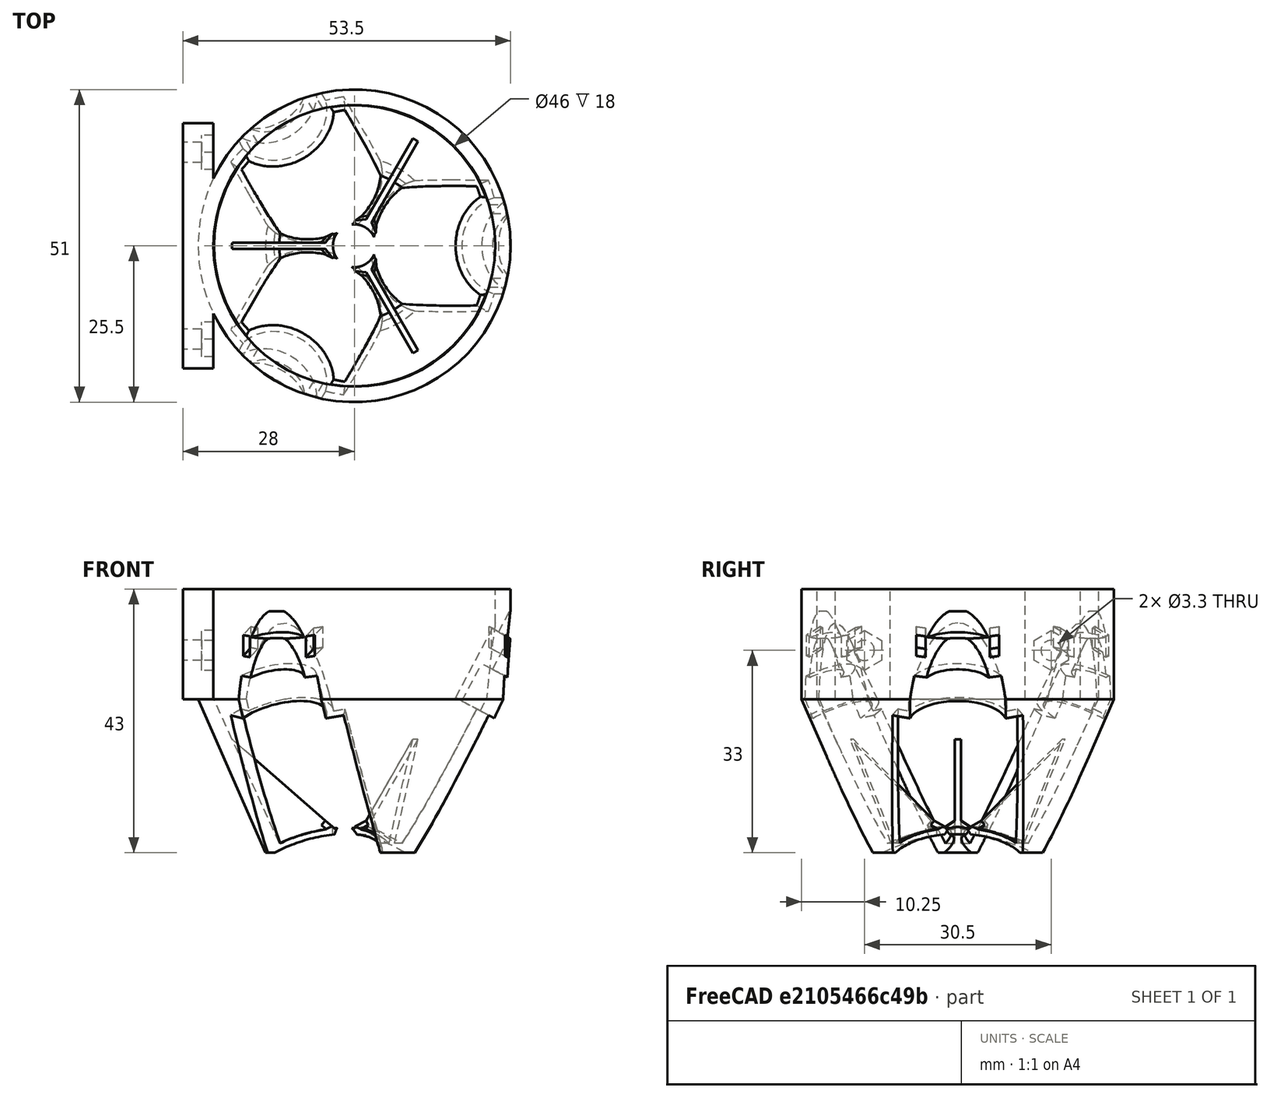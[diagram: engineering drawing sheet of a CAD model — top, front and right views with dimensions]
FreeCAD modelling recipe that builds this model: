
FCSTD DOCUMENT  (FreeCAD 0.19R)
Label: hotend-diamond
License: All rights reserved
LicenseURL: http://en.wikipedia.org/wiki/All_rights_reserved
objects: Part::Cylinder×26, Part::Fuse×13, Part::Box×13, Part::MultiFuse×12, Part::Cut×7, Part::Cone×2, Part::Sphere×2, Part::Prism×2, PartDesign::FeatureBase×1, PartDesign::Body×1
note: 79 computed .brp shape members not serialized (recipe doc carries the construction recipe); baked Part::Feature solids carry a one-line shape summary decoded from their .brp

FEATURE [Part::Cone] cylinder
  Angle = 360
  AttacherType = Attacher::AttachEngine3D
  Height = 25
  Radius1 = 14.5
  Radius2 = 25.5
FEATURE [Part::Sphere] sphere
  Angle1 = -90
  Angle2 = 90
  Angle3 = 360
  AttacherType = Attacher::AttachEngine3D
  Placement = pos=(0,0,-25.49) rot=(0,0,1;0rad)
  Radius = 28.6923
FEATURE [Part::Cylinder] cylinder001
  Angle = 360
  AttacherType = Attacher::AttachEngine3D
  Height = 2.39233
  Placement = pos=(0,0,2.19233) rot=(0,0,1;0rad)
  Radius = 3.5
FEATURE [Part::Cone] cylinder002
  Angle = 360
  AttacherType = Attacher::AttachEngine3D
  Height = 24.2
  Radius1 = 12
  Radius2 = 23
FEATURE [Part::Cylinder] cylinder003
  Angle = 360
  AttacherType = Attacher::AttachEngine3D
  Height = 17.75
  Placement = pos=(24.6003,0,46.2665) rot=(0,1,0;0.488692rad)
  Radius = 9.25
FEATURE [Part::Cylinder] cylinder004
  Angle = 360
  AttacherType = Attacher::AttachEngine3D
  Height = 17.75
  Placement = pos=(-12.3002,21.3045,46.2665) rot=(-0.239596,0.138331,0.960967;2.12853rad)
  Radius = 9.25
FEATURE [Part::Cylinder] cylinder005
  Angle = 360
  AttacherType = Attacher::AttachEngine3D
  Height = 17.75
  Placement = pos=(-12.3002,-21.3045,46.2665) rot=(-0.239596,-0.138331,0.960967;4.15466rad)
  Radius = 9.25
FEATURE [Part::MultiFuse] Group
  Placement = pos=(0,0,-26.49) rot=(0,0,1;0rad)
  Shapes = -> [cylinder003,cylinder004,cylinder005]
FEATURE [Part::Sphere] sphere001
  Angle1 = -90
  Angle2 = 90
  Angle3 = 360
  AttacherType = Attacher::AttachEngine3D
  Placement = pos=(0,0,-26.49) rot=(0,0,1;0rad)
  Radius = 29.6923
FEATURE [Part::Fuse] union
  Base = -> Group
  Tool = -> sphere001
FEATURE [Part::Cut] difference
  Base = -> cylinder002
  Tool = -> union
FEATURE [Part::Box] cube
  AttacherType = Attacher::AttachEngine3D
  Height = 100
  Length = 10
  Placement = pos=(0,0.5,0) rot=(0,0,1;3.14159rad)
  Width = 1
FEATURE [Part::Box] cube001
  AttacherType = Attacher::AttachEngine3D
  Height = 1
  Length = 3
  Placement = pos=(5e-16,2e-16,-2.12132) rot=(0.357407,-0.862856,-0.357407;1.71777rad)
  Width = 3
FEATURE [Part::Fuse] union001
  Base = -> cube
  Placement = pos=(-3.5,0,0) rot=(0,-1,0;0.855211rad)
  Tool = -> cube001
FEATURE [Part::Box] cube002
  AttacherType = Attacher::AttachEngine3D
  Height = 100
  Length = 10
  Placement = pos=(0,0.5,0) rot=(0,0,1;3.14159rad)
  Width = 1
FEATURE [Part::Box] cube003
  AttacherType = Attacher::AttachEngine3D
  Height = 1
  Length = 3
  Placement = pos=(5e-16,2e-16,-2.12132) rot=(0.357407,-0.862856,-0.357407;1.71777rad)
  Width = 3
FEATURE [Part::Fuse] union002
  Base = -> cube002
  Placement = pos=(1.75,-3.03109,0) rot=(0.403295,-0.232843,0.88495;2.19689rad)
  Tool = -> cube003
FEATURE [Part::Box] cube004
  AttacherType = Attacher::AttachEngine3D
  Height = 100
  Length = 10
  Placement = pos=(0,0.5,0) rot=(0,0,1;3.14159rad)
  Width = 1
FEATURE [Part::Box] cube005
  AttacherType = Attacher::AttachEngine3D
  Height = 1
  Length = 3
  Placement = pos=(5e-16,2e-16,-2.12132) rot=(0.357407,-0.862856,-0.357407;1.71777rad)
  Width = 3
FEATURE [Part::Fuse] union003
  Base = -> cube004
  Placement = pos=(1.75,3.03109,0) rot=(0.403295,0.232843,0.88495;4.08629rad)
  Tool = -> cube005
FEATURE [Part::MultiFuse] Group001
  Placement = pos=(0,0,3.19233) rot=(0,0,1;0rad)
  Shapes = -> [union001,union002,union003]
FEATURE [Part::Cut] difference001
  Base = -> difference
  Placement = pos=(0,0,1) rot=(0,0,1;0rad)
  Tool = -> Group001
FEATURE [Part::MultiFuse] union004
  Placement = pos=(0,0,-0.01) rot=(0,0,1;0rad)
  Shapes = -> [sphere,cylinder001,difference001]
FEATURE [Part::Cut] difference002
  Base = -> cylinder
  Placement = pos=(0,0,25.5) rot=(0,0,1;0rad)
  Tool = -> union004
FEATURE [Part::Cylinder] cylinder006
  Angle = 360
  AttacherType = Attacher::AttachEngine3D
  Height = 18
  Placement = pos=(0,0,50.5) rot=(0,0,1;0rad)
  Radius = 25.5
FEATURE [Part::Cylinder] cylinder007
  Angle = 360
  AttacherType = Attacher::AttachEngine3D
  Height = 20
  Placement = pos=(0,0,49.5) rot=(0,0,1;0rad)
  Radius = 23
FEATURE [Part::Cylinder] cylinder008
  Angle = 360
  AttacherType = Attacher::AttachEngine3D
  Height = 17.75
  Placement = pos=(24.6003,0,46.2665) rot=(0,1,0;0.488692rad)
  Radius = 9.25
FEATURE [Part::Cylinder] cylinder009
  Angle = 360
  AttacherType = Attacher::AttachEngine3D
  Height = 17.75
  Placement = pos=(-12.3002,21.3045,46.2665) rot=(-0.239596,0.138331,0.960967;2.12853rad)
  Radius = 9.25
FEATURE [Part::Cylinder] cylinder010
  Angle = 360
  AttacherType = Attacher::AttachEngine3D
  Height = 17.75
  Placement = pos=(-12.3002,-21.3045,46.2665) rot=(-0.239596,-0.138331,0.960967;4.15466rad)
  Radius = 9.25
FEATURE [Part::MultiFuse] Group002
  Shapes = -> [cylinder008,cylinder009,cylinder010]
FEATURE [Part::Cut] difference003
  Base = -> cylinder007
  Tool = -> Group002
FEATURE [Part::Cut] difference004
  Base = -> cylinder006
  Tool = -> difference003
FEATURE [Part::Box] cube006
  AttacherType = Attacher::AttachEngine3D
  Height = 18
  Length = 5
  Placement = pos=(-5,-20,-18) rot=(0,0,1;0rad)
  Width = 40
FEATURE [Part::Cylinder] cylinder011
  Angle = 360
  AttacherType = Attacher::AttachEngine3D
  Height = 6
  Radius = 1.65
FEATURE [Part::Prism] prism
  AttacherType = Attacher::AttachEngine3D
  Circumradius = 3.25
  FirstAngle = 0
  Height = 2
  Polygon = 6
  SecondAngle = 0
FEATURE [Part::Fuse] union005
  Base = -> cylinder011
  Placement = pos=(0.1,-15.25,-10) rot=(0,-1,0;1.5708rad)
  Tool = -> prism
FEATURE [Part::Cylinder] cylinder012
  Angle = 360
  AttacherType = Attacher::AttachEngine3D
  Height = 6
  Radius = 1.65
FEATURE [Part::Prism] prism001
  AttacherType = Attacher::AttachEngine3D
  Circumradius = 3.25
  FirstAngle = 0
  Height = 2
  Polygon = 6
  SecondAngle = 0
FEATURE [Part::Fuse] union006
  Base = -> cylinder012
  Placement = pos=(0.1,15.25,-10) rot=(0,-1,0;1.5708rad)
  Tool = -> prism001
FEATURE [Part::Fuse] Group003
  Base = -> union005
  Tool = -> union006
FEATURE [Part::Cut] difference005
  Base = -> cube006
  Placement = pos=(-23,0,68.5) rot=(0,0,1;0rad)
  Tool = -> Group003
FEATURE [Part::MultiFuse] union007
  Shapes = -> [difference002,difference004,difference005]
FEATURE [Part::Cylinder] cylinder013
  Angle = 360
  AttacherType = Attacher::AttachEngine3D
  Height = 26.2
  Radius = 11.1
FEATURE [Part::Cylinder] cylinder014
  Angle = 360
  AttacherType = Attacher::AttachEngine3D
  Height = 8.1
  Placement = pos=(0,0,-1) rot=(0,0,1;0rad)
  Radius = 8.1
FEATURE [Part::Cylinder] cylinder015
  Angle = 360
  AttacherType = Attacher::AttachEngine3D
  Height = 8
  Placement = pos=(0,0,-1) rot=(0,0,1;0rad)
  Radius = 6.1
FEATURE [Part::Cylinder] cylinder016
  Angle = 360
  AttacherType = Attacher::AttachEngine3D
  Height = 3.95
  Placement = pos=(0,0,5.9) rot=(0,0,1;0rad)
  Radius = 8.1
FEATURE [Part::Box] cube007
  AttacherType = Attacher::AttachEngine3D
  Height = 3.01
  Length = 16
  Placement = pos=(-16,-6.75,2.995) rot=(0,0,1;0rad)
  Width = 1.5
FEATURE [Part::Box] cube008
  AttacherType = Attacher::AttachEngine3D
  Height = 3.01
  Length = 16
  Placement = pos=(-16,5.25,2.995) rot=(0,0,1;0rad)
  Width = 1.5
FEATURE [Part::Fuse] Group004
  Base = -> cube007
  Tool = -> cube008
FEATURE [Part::MultiFuse] union008
  Placement = pos=(0,0,7) rot=(0,0,1;0rad)
  Shapes = -> [cylinder015,cylinder016,Group004]
FEATURE [Part::Fuse] union009
  Base = -> cylinder014
  Placement = pos=(0,0,26) rot=(0,0,1;0rad)
  Tool = -> union008
FEATURE [Part::Cylinder] cylinder017
  Angle = 360
  AttacherType = Attacher::AttachEngine3D
  Height = 4
  Placement = pos=(0,0,0) rot=(1,0,0;3.14159rad)
  Radius = 3
FEATURE [Part::MultiFuse] union010
  Placement = pos=(12.394,0,23.3098) rot=(0,1,0;0.488692rad)
  Shapes = -> [cylinder013,union009,cylinder017]
FEATURE [Part::Cylinder] cylinder018
  Angle = 360
  AttacherType = Attacher::AttachEngine3D
  Height = 26.2
  Radius = 11.1
FEATURE [Part::Cylinder] cylinder019
  Angle = 360
  AttacherType = Attacher::AttachEngine3D
  Height = 8.1
  Placement = pos=(0,0,-1) rot=(0,0,1;0rad)
  Radius = 8.1
FEATURE [Part::Cylinder] cylinder020
  Angle = 360
  AttacherType = Attacher::AttachEngine3D
  Height = 8
  Placement = pos=(0,0,-1) rot=(0,0,1;0rad)
  Radius = 6.1
FEATURE [Part::Cylinder] cylinder021
  Angle = 360
  AttacherType = Attacher::AttachEngine3D
  Height = 3.95
  Placement = pos=(0,0,5.9) rot=(0,0,1;0rad)
  Radius = 8.1
FEATURE [Part::Box] cube009
  AttacherType = Attacher::AttachEngine3D
  Height = 3.01
  Length = 16
  Placement = pos=(-16,-6.75,2.995) rot=(0,0,1;0rad)
  Width = 1.5
FEATURE [Part::Box] cube010
  AttacherType = Attacher::AttachEngine3D
  Height = 3.01
  Length = 16
  Placement = pos=(-16,5.25,2.995) rot=(0,0,1;0rad)
  Width = 1.5
FEATURE [Part::Fuse] Group005
  Base = -> cube009
  Tool = -> cube010
FEATURE [Part::MultiFuse] union011
  Placement = pos=(0,0,7) rot=(0,0,1;0rad)
  Shapes = -> [cylinder020,cylinder021,Group005]
FEATURE [Part::Fuse] union012
  Base = -> cylinder019
  Placement = pos=(0,0,26) rot=(0,0,1;0rad)
  Tool = -> union011
FEATURE [Part::Cylinder] cylinder022
  Angle = 360
  AttacherType = Attacher::AttachEngine3D
  Height = 4
  Placement = pos=(0,0,0) rot=(1,0,0;3.14159rad)
  Radius = 3
FEATURE [Part::MultiFuse] union013
  Placement = pos=(-6.19702,10.7336,23.3098) rot=(-0.239596,0.138331,0.960967;2.12853rad)
  Shapes = -> [cylinder018,union012,cylinder022]
FEATURE [Part::Cylinder] cylinder023
  Angle = 360
  AttacherType = Attacher::AttachEngine3D
  Height = 26.2
  Radius = 11.1
FEATURE [Part::Cylinder] cylinder024
  Angle = 360
  AttacherType = Attacher::AttachEngine3D
  Height = 8.1
  Placement = pos=(0,0,-1) rot=(0,0,1;0rad)
  Radius = 8.1
FEATURE [Part::Cylinder] cylinder025
  Angle = 360
  AttacherType = Attacher::AttachEngine3D
  Height = 8
  Placement = pos=(0,0,-1) rot=(0,0,1;0rad)
  Radius = 6.1
FEATURE [Part::Cylinder] cylinder026
  Angle = 360
  AttacherType = Attacher::AttachEngine3D
  Height = 3.95
  Placement = pos=(0,0,5.9) rot=(0,0,1;0rad)
  Radius = 8.1
FEATURE [Part::Box] cube011
  AttacherType = Attacher::AttachEngine3D
  Height = 3.01
  Length = 16
  Placement = pos=(-16,-6.75,2.995) rot=(0,0,1;0rad)
  Width = 1.5
FEATURE [Part::Box] cube012
  AttacherType = Attacher::AttachEngine3D
  Height = 3.01
  Length = 16
  Placement = pos=(-16,5.25,2.995) rot=(0,0,1;0rad)
  Width = 1.5
FEATURE [Part::Fuse] Group006
  Base = -> cube011
  Tool = -> cube012
FEATURE [Part::MultiFuse] union014
  Placement = pos=(0,0,7) rot=(0,0,1;0rad)
  Shapes = -> [cylinder025,cylinder026,Group006]
FEATURE [Part::Fuse] union015
  Base = -> cylinder024
  Placement = pos=(0,0,26) rot=(0,0,1;0rad)
  Tool = -> union014
FEATURE [Part::Cylinder] cylinder027
  Angle = 360
  AttacherType = Attacher::AttachEngine3D
  Height = 4
  Placement = pos=(0,0,0) rot=(1,0,0;3.14159rad)
  Radius = 3
FEATURE [Part::MultiFuse] union016
  Placement = pos=(-6.19702,-10.7336,23.3098) rot=(-0.239596,-0.138331,0.960967;4.15466rad)
  Shapes = -> [cylinder023,union015,cylinder027]
FEATURE [Part::MultiFuse] Group007
  Shapes = -> [union010,union013,union016]
FEATURE [Part::Cut] difference006
  Base = -> union007
  Placement = pos=(0,8.4e-15,68.5) rot=(1,0,0;3.14159rad)
  Refine = true
  Tool = -> Group007
FEATURE [PartDesign::FeatureBase] BaseFeature
  BaseFeature = -> difference006
FEATURE [PartDesign::Body] Body
  BaseFeature = -> difference006
  Group = -> [BaseFeature]
  Origin = -> Origin
  Tip = -> BaseFeature
